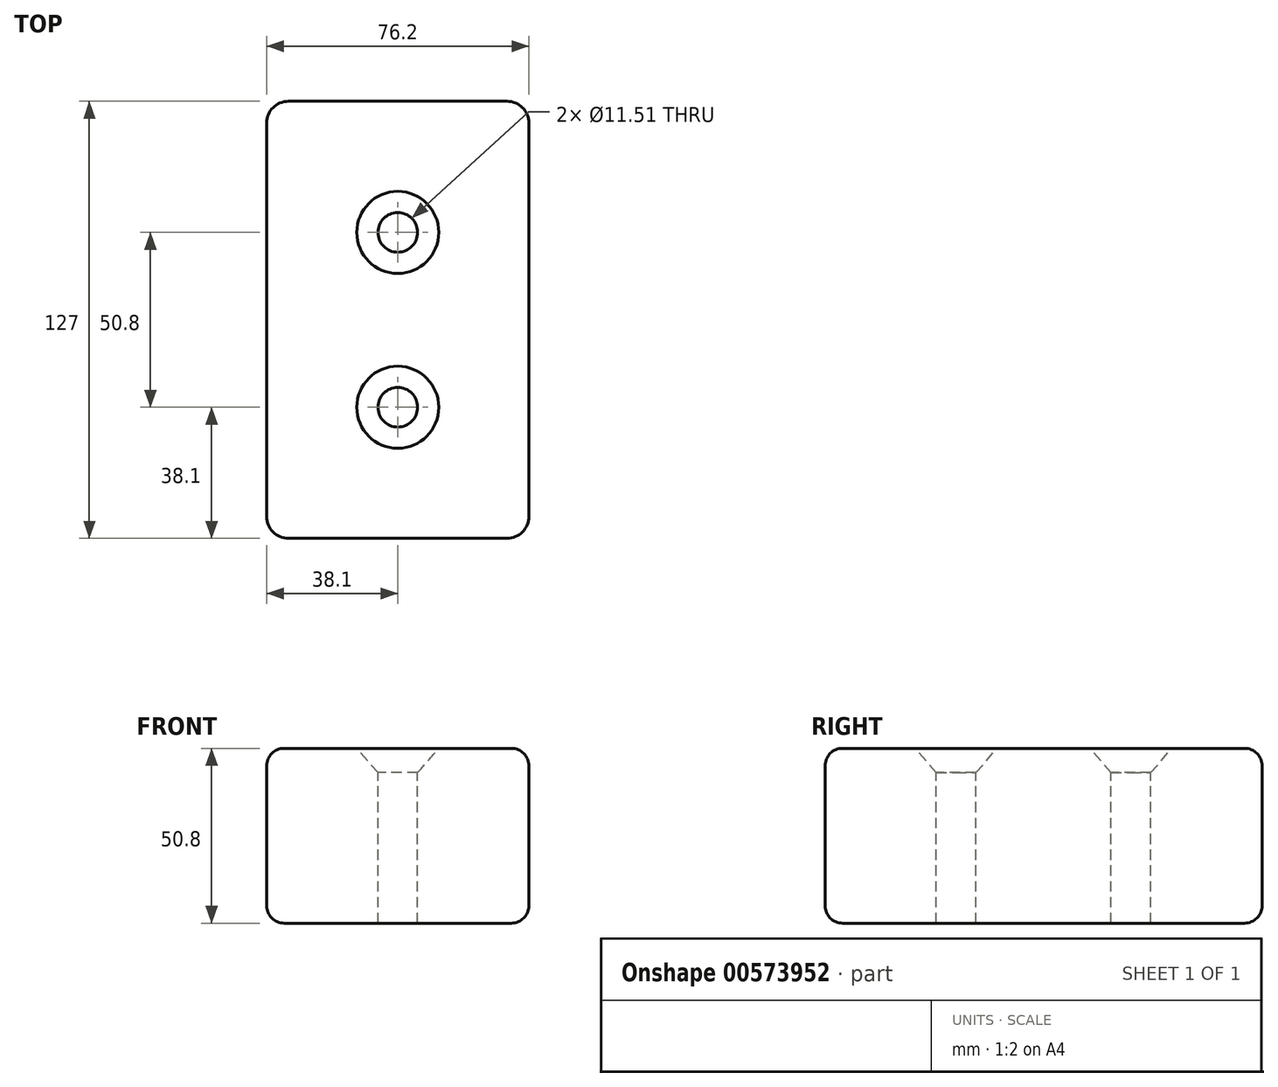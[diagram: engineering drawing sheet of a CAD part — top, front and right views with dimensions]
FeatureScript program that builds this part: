
annotation { "Feature Type Name" : "Feature", "Feature Type Description" : "" }
export const myFeature = defineFeature(function(context is Context, id is Id, definition is map)
    precondition{}
    {
        {
            var Q0;
            Q0=qCreatedBy(makeId("Top.planeOp"),FACE);
            var sketch = newSketch(context, id + "F0", { "sketchPlane" : qUnion([Q0])});
            skLineSegment(sketch, "E0.bottom", {"start": v(-38.1, 63.5) * mm, "end": v(38.1, 63.5) * mm});
            skLineSegment(sketch, "E0.top", {"start": v(-38.1, -63.5) * mm, "end": v(38.1, -63.5) * mm});
            skLineSegment(sketch, "E0.left", {"start": v(-38.1, 63.5) * mm, "end": v(-38.1, -63.5) * mm});
            skLineSegment(sketch, "E0.right", {"start": v(38.1, 63.5) * mm, "end": v(38.1, -63.5) * mm});
            skPoint(sketch, "E0.middle", {"position": v(0, 0) * mm});
            skSolve(sketch);
        }
        {
            var Q0;
            Q0=makeQuery(id+"F0.imprint","IMPRINT",FACE,{"disambiguationData":[TD([[makeQuery(id+"F0.imprint","IMPRINT",EDGE,{"derivedFrom":sQuery(id+"F0.wireOp",EDGE,"E0.bottom")}),-1.0]])]});
            extrude(context, id + "F1", {"entities" : qUnion([Q0]), "endBound" : BoundingType.SYMMETRIC, "depth" : 50.8 * mm, "offsetDistance" : 25.4 * mm});
        }
        {
            var Q0;
            Q0=makeQuery(id+"F1.opExtrude","SWEPT_EDGE",EDGE,{"disambiguationData":[OSD([sQuery(id+"F0.wireOp",EDGE,"E0.top"),sQuery(id+"F0.wireOp",EDGE,"E0.right")])]});
            var Q1;
            Q1=makeQuery(id+"F1.opExtrude","SWEPT_EDGE",EDGE,{"disambiguationData":[OSD([sQuery(id+"F0.wireOp",EDGE,"E0.bottom"),sQuery(id+"F0.wireOp",EDGE,"E0.right")])]});
            var Q2;
            Q2=makeQuery(id+"F1.opExtrude","SWEPT_EDGE",EDGE,{"disambiguationData":[OSD([sQuery(id+"F0.wireOp",EDGE,"E0.top"),sQuery(id+"F0.wireOp",EDGE,"E0.left")])]});
            var Q3;
            Q3=makeQuery(id+"F1.opExtrude","SWEPT_EDGE",EDGE,{"disambiguationData":[OSD([sQuery(id+"F0.wireOp",EDGE,"E0.bottom"),sQuery(id+"F0.wireOp",EDGE,"E0.left")])]});
            fillet(context, id + "F2", {"entities" : qUnion([Q0, Q1, Q2, Q3]), "radius" : 6.35 * mm, "tangentPropagation" : true, "allowEdgeOverflow" : false});
        }
        {
            var Q0;
            Q0=makeQuery(id+"F1.opExtrude","CAP_FACE",FACE,{"disambiguationData":[OSD([sQuery(id+"F0.wireOp",EDGE,"E0.bottom"),sQuery(id+"F0.wireOp",EDGE,"E0.top"),sQuery(id+"F0.wireOp",EDGE,"E0.left"),sQuery(id+"F0.wireOp",EDGE,"E0.right")])],"isStart":false});
            var sketch = newSketch(context, id + "F3", { "sketchPlane" : qUnion([Q0])});
            skPoint(sketch, "E1", {"position": v(0, -25.4) * mm});
            skPoint(sketch, "E2", {"position": v(0, 25.4) * mm});
            skLineSegment(sketch, "E3", {"start": v(0, -63.5) * mm, "end": v(0, 63.5) * mm, "construction": true});
            skSolve(sketch);
        }
        {
            var Q0;
            Q0=sQuery(id+"F3.wireOp",VERTEX,"E1");
            var Q1;
            Q1=sQuery(id+"F3.wireOp",VERTEX,"E2");
            var Q2;
            Q2=makeQuery(id+"F1.opExtrude","SWEPT_BODY",BODY,{"disambiguationData":[OSD([sQuery(id+"F0.wireOp",EDGE,"E0.bottom"),sQuery(id+"F0.wireOp",EDGE,"E0.top"),sQuery(id+"F0.wireOp",EDGE,"E0.left"),sQuery(id+"F0.wireOp",EDGE,"E0.right")])]});
            hole(context, id + "F4", {"style" : HoleStyle.C_SINK, "endStyle" : HoleEndStyle.THROUGH, "standardTappedOrClearance" : lookupTablePath({ "standard" : "ANSI", "engagement" : "75%", "pitch" : "20 tpi", "size" : "1/2", "type" : "Tapped" }), "standardBlindInLast" : lookupTablePath({ "standard" : "ANSI", "engagement" : "75%", "pitch" : "20 tpi", "size" : "1/2", "type" : "Tapped" }), "holeDiameter" : 11.5 * mm, "cSinkDiameter" : 23.83 * mm, "cSinkAngle" : 82 * degree, "showTappedDepth" : true, "isTappedThrough" : true, "tappedDepth" : 12.7 * mm, "tapClearance" : 3, "locations" : qUnion([Q0, Q1]), "scope" : qUnion([Q2]), "majorDiameter" : 12.7 * mm});
        }
        {
            var Q0;
            Q0=makeQuery(id+"F1.opExtrude","CAP_EDGE",EDGE,{"disambiguationData":[OSD([sQuery(id+"F0.wireOp",EDGE,"E0.right")])],"isStart":false});
            var Q1;
            Q1=makeQuery(id+"F1.opExtrude","CAP_EDGE",EDGE,{"disambiguationData":[OSD([sQuery(id+"F0.wireOp",EDGE,"E0.right")])],"isStart":true});
            fillet(context, id + "F5", {"entities" : qUnion([Q0, Q1]), "radius" : 5.08 * mm, "tangentPropagation" : true, "allowEdgeOverflow" : false});
        }
    });
